# Revit family: TataSteel_Lintels_TS_110-125_100-115
name_source: partatom
category: Generic Models
revit_build: Autodesk Revit 2015 (Build: 20140606_1530(x64)
units: mm (PartAtom-declared; Revit-internal decimal feet)

## types (1)
- TataSteel_Lintels_TS_110-125_100-115
    AllowableLoadLimiting = 26 mm
    AssetType = FIXED
    BIMObjectName = TataSteel_Lintel_TS110_100_2700
    BIMobject category = Beams & Lintels
    CharacteristicDeflectionUnderLoad = 0 mm  [stored 0 ft]
    CharacteristicResistanceToFire = 60 mm  [stored 0.19685 ft]
    CharacteristicThermalConductivity = 0 mm  [stored 0 ft]
    ClearSpan = 2400 mm
    Color = Black
    Description = Standard duty thermally broken cavity wall lintel
    Edition number = 1
    EndBearing = 150 mm  [stored 0.492126 ft]
    ExpectedLife = 60 yrs
    Finish = Galv and Powder coated
    FireRating = 60
    Grade = DX51
    IFC Classification = Structural Member
    IfcExportAs = IfcBeamType
    IfcExportType = LINTEL
    Installation instructions = http://catnic.com
    InstallationDate = 1900-12-31T23:59:59
    Insulation = Insulation
    IsExternal = Yes
    LengthIncrement = 150mm up to 3000mm. 
300mm above 3000mm
    LintelAngle = 26.00°
    LintelCavity = 110 mm  [stored 0.360892 ft]
    LintelFront1 = 129 mm  [stored 0.423228 ft]
    LintelFront2 = 197 mm
    LintelHeight = 233 mm  [stored 0.764436 ft]
    LintelInnerLeaf = 100 mm  [stored 0.328084 ft]
    LintelLength = 2700 mm  [stored 8.85827 ft]
    LintelOuterLeaf = 95 mm
    LintelThickness = 3 mm  [stored 0.00984252 ft]
    LintelType = CAVITY
    Lip = 2 mm  [stored 0.00656168 ft]
    LoadBearing = Yes
    LoadCategory = STANDARD DUTY
    Manufacturer = Catnic, TATA
    Manufacturer country = United Kingdom
    Manufacturer name = Tata Steel
    ManufacturerURL = www.catnic.com
    Material = Galvanised Steel
    Material main = Steel
    MaxLintelLength = 3600
    MinLintelLength = 750
    Model = TataSteel_Lintel_TS110_100_2700
    ModelNumber = TS
    ModelReference = Cavity Walls
    NBSDescription = Pre fabricated Steel Lintel
    NBSReference = F30 755
    Name = Lintel
    Nominal height = 0
    Nominal width = 0
    NominalLength = 2700 mm  [stored 8.85827 ft]
    OmniClass Code = 23-13 21 25 11
    OmniClass Description = Lintels
    Product Guid = bebfd9c8-5d14-455e-8b35-0cf6c048abb3
    Product SKU = catnic-ts
    Product certification = http://catnic.com
    Product family = Lintels
    Product group = Catnic
    ProductInformation = www.catnic.com
    QR code = http://bimobject.com
    Roll = 0 mm  [stored 0 ft]
    SafeWorkingLoad = 26 mm
    Shape = Open back lintel
    Size = 233H x312W x2700L
    Slope = 0 mm  [stored 0 ft]
    Span = 2400 mm
    Steel = Steel
    TSE_BIMObjectName = TataSteel_Lintel_TS110_100_2700
    TSE_Description = Catnic’s latest innovation is the biggest shake up in steel lintel design for a generation. An elegant, simplistic design derived from extensive research and rigorous development testing, offering a sophisticated, practical solution to the latest changes in Building Regulations. TBL is a patent pending range providing the most thermally efficient steel lintel solution on the market.
    TSE_Documentation = www.catnic.com
    TSE_InstallationInstructions = www.catnic.com
    TSE_ManufacturerURL = www.catnic.com
    TSE_Model = TataSteel_Lintel_TS110_100_2700
    TSE_ProductCertification = www.catnic.com
    TSE_QR code = <None>
    Technical description = http://catnic.com
    ThermalTransmittance = 0 mm  [stored 0 ft]
    Type Image = <None>
    UNSPSC Code = 30101704
    URL = www.catnic.com
    Uniclass 1.4 Code = L3241
    Uniclass 1.4 Description = Lintels
    Uniclass 2015 Code = Pr_20_85_48
    Uniclass 2015 Name = Lintels
    Uniclass2015 = Pr_20_85_48_11
    WallCavity = 110 mm  [stored 0.360892 ft]
    WallCavityRange = 110-125
    WallInnerLeaf = 100 mm  [stored 0.328084 ft]
    WallInnerLeafRange = 100-115
    WallOuterLeaf = 102 mm
    WarrantyStartDate = 1900-12-31T23:59:59
    Weight = 16 mm
    Weight Net (Kg) = 0
    b1 = 150 mm  [stored 0.492126 ft]
    b2 = 155 mm
    b3 = 55 mm  [stored 0.180446 ft]

note: [stored X ft] marks values corroborated as IEEE doubles in the binary element streams (Revit-internal decimal feet)

## geometry (parser evidence)
native form markers: Sweep x3
no freeform markers — native parametric forms only
